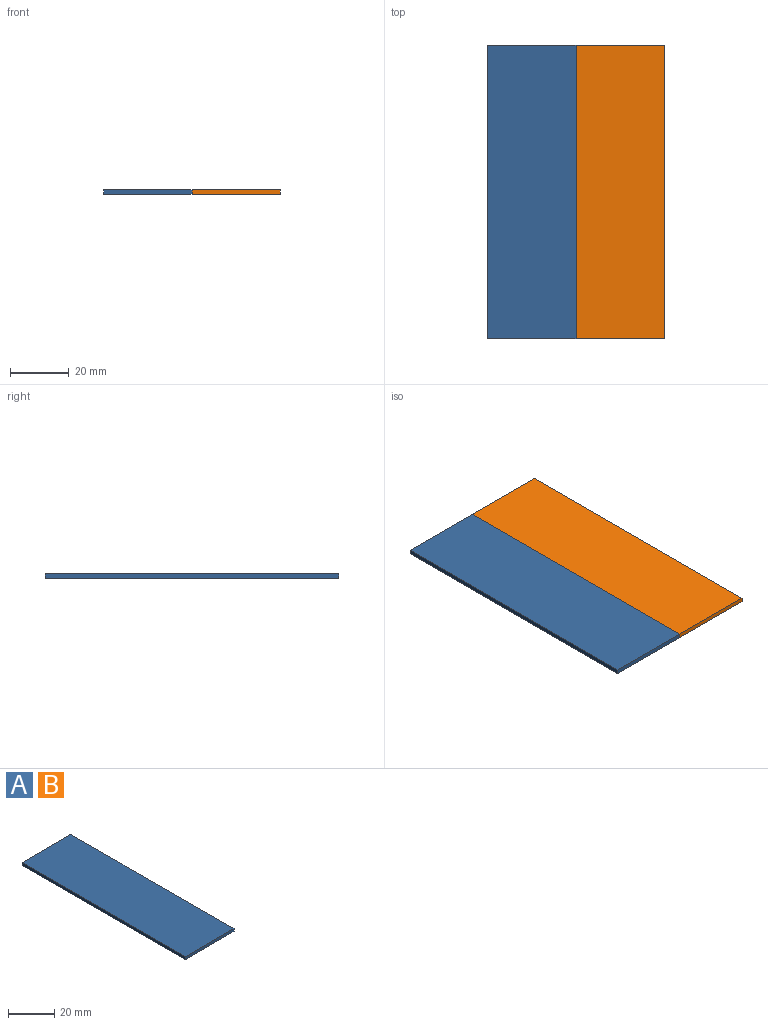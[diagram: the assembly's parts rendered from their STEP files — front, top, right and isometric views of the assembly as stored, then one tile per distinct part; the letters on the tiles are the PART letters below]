
ASSEMBLY  parts=2 mates=1
PART A: 6 faces, bbox 30x100x1.5 mm
  f0: plane 30x1.5mm, normal (0,-1,0), area 45mm2, adj f1,f3,f4,f5
  f1: plane 100x1.5mm, normal (1,0,0), area 150mm2, adj f0,f2,f4,f5
  f2: plane 30x1.5mm, normal (0,1,0), area 45mm2, adj f1,f3,f4,f5
  f3: plane 100x1.5mm, normal (-1,0,0), area 150mm2, adj f0,f2,f4,f5
  f4: plane 100x30mm, normal (0,0,1), area 3000mm2, adj f0,f1,f2,f3
  f5: plane 100x30mm, normal (0,0,-1), area 3000mm2, adj f0,f1,f2,f3
PART B: same geometry as A
PLACE A t=(0.97,-5.67,-17.3)mm
PLACE B rot(axis=(0,1,0),0deg) t=(30.97,-5.67,-17.3)mm
MATE parallel B.f3 <-> A.f1  axis (-1,0,0) through (15.97,-5.67,-16.55)mm
